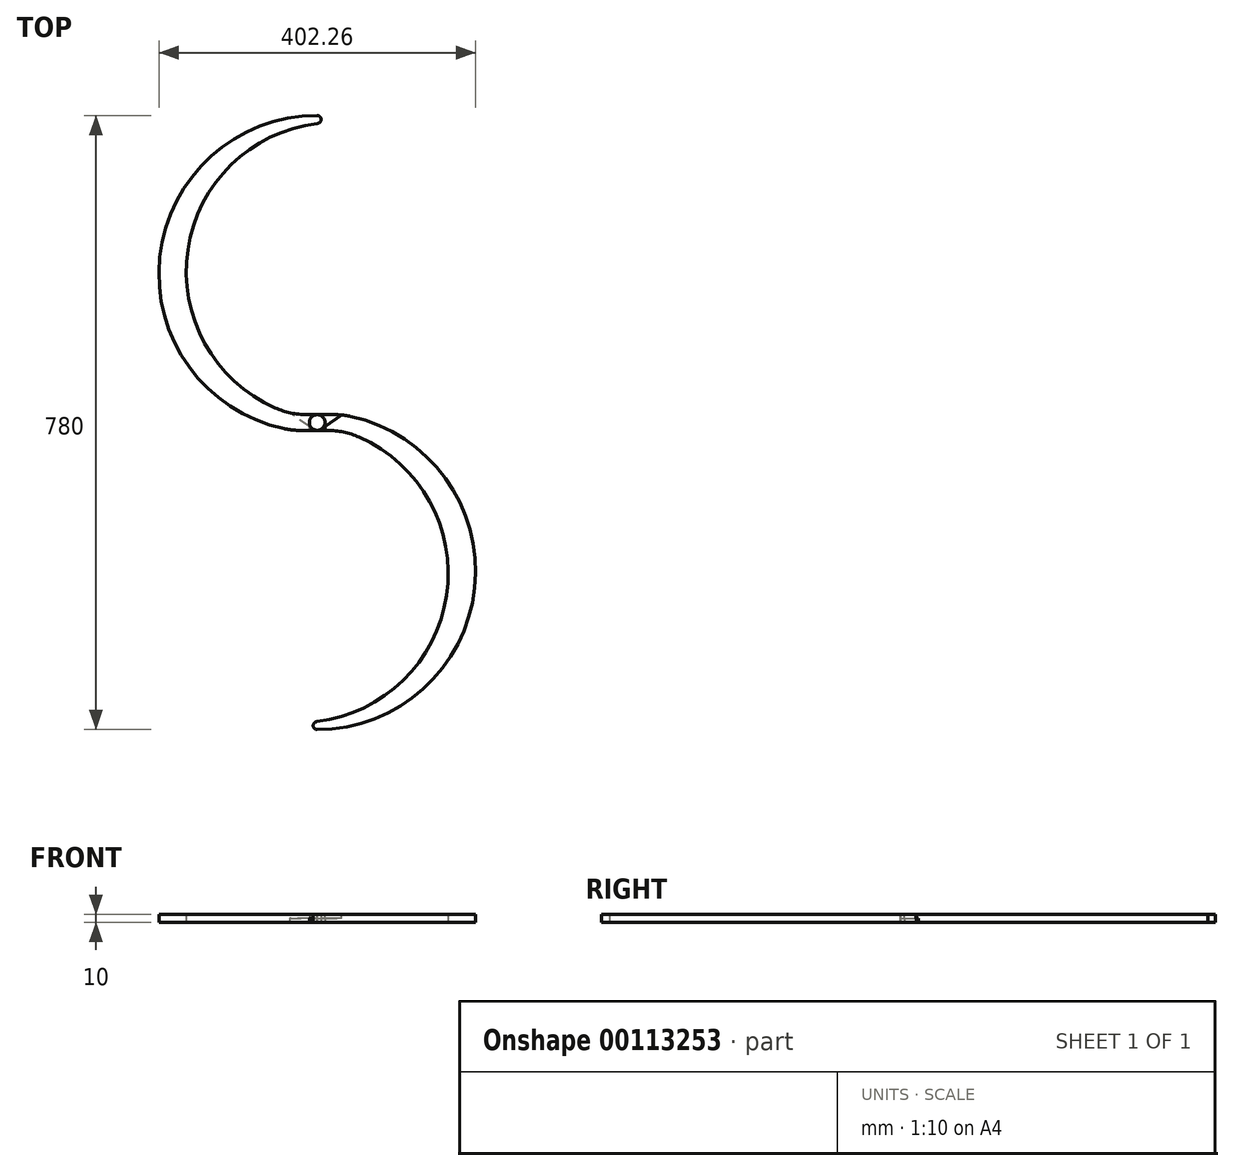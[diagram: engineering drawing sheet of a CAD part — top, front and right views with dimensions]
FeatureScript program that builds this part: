
annotation { "Feature Type Name" : "Feature", "Feature Type Description" : "" }
export const myFeature = defineFeature(function(context is Context, id is Id, definition is map)
    precondition{}
    {
        {
            var Q0;
            Q0=qCreatedBy(makeId("Top.planeOp"),FACE);
            var sketch = newSketch(context, id + "F0", { "sketchPlane" : qUnion([Q0])});
            skArc(sketch, "E0", {"start": v(0, 390) * mm, "mid": v(-200, 210.09) * mm, "end": v(-42.2, -7.78) * mm});
            skLineSegment(sketch, "E1", {"start": v(-21.21, -10) * mm, "end": v(0, -10) * mm});
            skLineSegment(sketch, "E2", {"start": v(0, -10) * mm, "end": v(0, 10) * mm, "construction": true});
            skPoint(sketch, "E3", {"position": v(0, 0) * mm});
            skLineSegment(sketch, "E4", {"start": v(0, 10) * mm, "end": v(-12.94, 10) * mm});
            skArc(sketch, "E5", {"start": v(0, 380) * mm, "mid": v(-164.3, 219.56) * mm, "end": v(-53.31, 18.51) * mm});
            skArc(sketch, "E6", {"start": v(0, 380) * mm, "mid": v(5, 385) * mm, "end": v(0, 390) * mm});
            skArc(sketch, "E7.1.0", {"start": v(0, -390) * mm, "mid": v(200, -210.09) * mm, "end": v(42.2, 7.78) * mm});
            skArc(sketch, "E7.1.1", {"start": v(0, -380) * mm, "mid": v(164.3, -219.56) * mm, "end": v(53.31, -18.51) * mm});
            skArc(sketch, "E7.1.2", {"start": v(0, -380) * mm, "mid": v(-5, -385) * mm, "end": v(0, -390) * mm});
            skLineSegment(sketch, "E7.1.3", {"start": v(0, -10) * mm, "end": v(12.94, -10) * mm});
            skLineSegment(sketch, "E7.1.4", {"start": v(21.21, 10) * mm, "end": v(0, 10) * mm});
            skPoint(sketch, "E8.visualSharp", {"position": v(-30, 10) * mm});
            skArc(sketch, "E8.filletArc", {"start": v(-53.31, 18.51) * mm, "mid": v(-33.57, 12.15) * mm, "end": v(-12.94, 10) * mm});
            skPoint(sketch, "E9.visualSharp", {"position": v(30, 10) * mm});
            skArc(sketch, "E9.filletArc", {"start": v(42.2, 7.78) * mm, "mid": v(31.76, 9.44) * mm, "end": v(21.21, 10) * mm});
            skPoint(sketch, "E10.visualSharp", {"position": v(-30, -10) * mm});
            skArc(sketch, "E10.filletArc", {"start": v(-42.2, -7.78) * mm, "mid": v(-31.76, -9.44) * mm, "end": v(-21.21, -10) * mm});
            skPoint(sketch, "E11.visualSharp", {"position": v(30, -10) * mm});
            skArc(sketch, "E11.filletArc", {"start": v(53.31, -18.51) * mm, "mid": v(33.57, -12.15) * mm, "end": v(12.94, -10) * mm});
            skLineSegment(sketch, "E12.bottom", {"start": v(47.12, -23.38) * mm, "end": v(-234.9, -23.38) * mm, "construction": true});
            skLineSegment(sketch, "E12.top", {"start": v(47.12, 411.9) * mm, "end": v(-234.9, 411.9) * mm, "construction": true});
            skLineSegment(sketch, "E12.left", {"start": v(47.12, -23.38) * mm, "end": v(47.12, 411.9) * mm, "construction": true});
            skLineSegment(sketch, "E12.right", {"start": v(-234.9, -23.38) * mm, "end": v(-234.9, 411.9) * mm, "construction": true});
            skSolve(sketch);
        }
        {
            var Q0;
            Q0=qSketchRegion(id+"F0",true);
            extrude(context, id + "F1", {"entities" : qUnion([Q0]), "depth" : 10 * mm});
        }
        {
            var Q0;
            Q0=makeQuery(id+"F1.opExtrude","CAP_FACE",FACE,{"disambiguationData":[OSD([sQuery(id+"F0.wireOp",EDGE,"E0"),sQuery(id+"F0.wireOp",EDGE,"E1"),sQuery(id+"F0.wireOp",EDGE,"E4"),sQuery(id+"F0.wireOp",EDGE,"E5"),sQuery(id+"F0.wireOp",EDGE,"E6"),sQuery(id+"F0.wireOp",EDGE,"E7.1.0"),sQuery(id+"F0.wireOp",EDGE,"E7.1.1"),sQuery(id+"F0.wireOp",EDGE,"E7.1.2"),sQuery(id+"F0.wireOp",EDGE,"E7.1.3"),sQuery(id+"F0.wireOp",EDGE,"E7.1.4"),sQuery(id+"F0.wireOp",EDGE,"E8.filletArc"),sQuery(id+"F0.wireOp",EDGE,"E9.filletArc"),sQuery(id+"F0.wireOp",EDGE,"E10.filletArc"),sQuery(id+"F0.wireOp",EDGE,"E11.filletArc")])],"isStart":false});
            var sketch = newSketch(context, id + "F2", { "sketchPlane" : qUnion([Q0])});
            skCircle(sketch, "E13", {"center": v(0, 0) * mm, "radius": 3 * mm});
            skArc(sketch, "E14", {"start": v(0, -10) * mm, "mid": v(10, 0) * mm, "end": v(0, 10) * mm});
            skLineSegment(sketch, "E15.0", {"start": v(21.21, 10) * mm, "end": v(-12.94, 10) * mm});
            skArc(sketch, "E16.0", {"start": v(42.2, 7.78) * mm, "mid": v(31.76, 9.44) * mm, "end": v(21.21, 10) * mm});
            skArc(sketch, "E17.0", {"start": v(0, -390) * mm, "mid": v(200, -210.09) * mm, "end": v(42.2, 7.78) * mm});
            skArc(sketch, "E18.0", {"start": v(0, -380) * mm, "mid": v(-5, -385) * mm, "end": v(0, -390) * mm});
            skArc(sketch, "E19.0", {"start": v(0, -380) * mm, "mid": v(164.3, -219.56) * mm, "end": v(53.31, -18.51) * mm});
            skArc(sketch, "E20.0", {"start": v(53.31, -18.51) * mm, "mid": v(33.57, -12.15) * mm, "end": v(12.94, -10) * mm});
            skLineSegment(sketch, "E21.0", {"start": v(-21.21, -10) * mm, "end": v(12.94, -10) * mm});
            skSolve(sketch);
        }
        {
            var Q0;
            Q0 = qSketchRegion(id + "F2", true);
            extrude(context, id + "F3", {"entities" : qUnion([Q0]), "operationType" : NewBodyOperationType.REMOVE, "oppositeDirection" : true, "depth" : 25 * mm});
        }
        {
            var Q0;
            Q0=makeQuery(id+"F1.opExtrude","SWEPT_BODY",BODY,{"disambiguationData":[OSD([sQuery(id+"F0.wireOp",EDGE,"E0"),sQuery(id+"F0.wireOp",EDGE,"E1"),sQuery(id+"F0.wireOp",EDGE,"E4"),sQuery(id+"F0.wireOp",EDGE,"E5"),sQuery(id+"F0.wireOp",EDGE,"E6"),sQuery(id+"F0.wireOp",EDGE,"E7.1.0"),sQuery(id+"F0.wireOp",EDGE,"E7.1.1"),sQuery(id+"F0.wireOp",EDGE,"E7.1.2"),sQuery(id+"F0.wireOp",EDGE,"E7.1.3"),sQuery(id+"F0.wireOp",EDGE,"E7.1.4"),sQuery(id+"F0.wireOp",EDGE,"E8.filletArc"),sQuery(id+"F0.wireOp",EDGE,"E9.filletArc"),sQuery(id+"F0.wireOp",EDGE,"E10.filletArc"),sQuery(id+"F0.wireOp",EDGE,"E11.filletArc")])]});
            var Q1;
            Q1=qCreatedBy(makeId("Right.planeOp"),FACE);
            mirror(context, id + "F4", {"entities" : qUnion([Q0]), "mirrorPlane" : qUnion([Q1])});
        }
        {
            var Q0;
            Q0=makeQuery(id+"F1.opExtrude","CAP_FACE",FACE,{"disambiguationData":[OSD([sQuery(id+"F0.wireOp",EDGE,"E0"),sQuery(id+"F0.wireOp",EDGE,"E1"),sQuery(id+"F0.wireOp",EDGE,"E4"),sQuery(id+"F0.wireOp",EDGE,"E5"),sQuery(id+"F0.wireOp",EDGE,"E6"),sQuery(id+"F0.wireOp",EDGE,"E7.1.0"),sQuery(id+"F0.wireOp",EDGE,"E7.1.1"),sQuery(id+"F0.wireOp",EDGE,"E7.1.2"),sQuery(id+"F0.wireOp",EDGE,"E7.1.3"),sQuery(id+"F0.wireOp",EDGE,"E7.1.4"),sQuery(id+"F0.wireOp",EDGE,"E8.filletArc"),sQuery(id+"F0.wireOp",EDGE,"E9.filletArc"),sQuery(id+"F0.wireOp",EDGE,"E10.filletArc"),sQuery(id+"F0.wireOp",EDGE,"E11.filletArc")])],"isStart":true});
            var sketch = newSketch(context, id + "F5", { "sketchPlane" : qUnion([Q0])});
            skCircle(sketch, "E22", {"center": v(0, 0) * mm, "radius": 10 * mm});
            skLineSegment(sketch, "E23", {"start": v(-5.74, 8.2) * mm, "end": v(-35.35, -12.54) * mm});
            skArc(sketch, "E24.0", {"start": v(-53.31, -18.51) * mm, "mid": v(-33.57, -12.15) * mm, "end": v(-12.94, -10) * mm});
            skLineSegment(sketch, "E25.0", {"start": v(0, -10) * mm, "end": v(-12.94, -10) * mm});
            skSolve(sketch);
        }
        {
            var Q0;
            Q0 = qSketchRegion(id + "F5", true);
            extrude(context, id + "F6", {"entities" : qUnion([Q0]), "operationType" : NewBodyOperationType.REMOVE, "oppositeDirection" : true, "depth" : 5 * mm});
        }
        {
            var Q0;
            Q0=makeQuery(id+"F4.opPattern","COPY",BODY,{"derivedFrom":makeQuery(id+"F1.opExtrude","SWEPT_BODY",BODY,{"disambiguationData":[OSD([sQuery(id+"F0.wireOp",EDGE,"E0"),sQuery(id+"F0.wireOp",EDGE,"E1"),sQuery(id+"F0.wireOp",EDGE,"E4"),sQuery(id+"F0.wireOp",EDGE,"E5"),sQuery(id+"F0.wireOp",EDGE,"E6"),sQuery(id+"F0.wireOp",EDGE,"E7.1.0"),sQuery(id+"F0.wireOp",EDGE,"E7.1.1"),sQuery(id+"F0.wireOp",EDGE,"E7.1.2"),sQuery(id+"F0.wireOp",EDGE,"E7.1.3"),sQuery(id+"F0.wireOp",EDGE,"E7.1.4"),sQuery(id+"F0.wireOp",EDGE,"E8.filletArc"),sQuery(id+"F0.wireOp",EDGE,"E9.filletArc"),sQuery(id+"F0.wireOp",EDGE,"E10.filletArc"),sQuery(id+"F0.wireOp",EDGE,"E11.filletArc")])]}),"instanceName":"1"});
            var Q1;
            Q1=qCreatedBy(makeId("Front.planeOp"),FACE);
            mirror(context, id + "F7", {"entities" : qUnion([Q0]), "mirrorPlane" : qUnion([Q1])});
        }
        {
            var Q0;
            Q0=makeQuery(id+"F4.opPattern","COPY",BODY,{"derivedFrom":makeQuery(id+"F1.opExtrude","SWEPT_BODY",BODY,{"disambiguationData":[OSD([sQuery(id+"F0.wireOp",EDGE,"E0"),sQuery(id+"F0.wireOp",EDGE,"E1"),sQuery(id+"F0.wireOp",EDGE,"E4"),sQuery(id+"F0.wireOp",EDGE,"E5"),sQuery(id+"F0.wireOp",EDGE,"E6"),sQuery(id+"F0.wireOp",EDGE,"E7.1.0"),sQuery(id+"F0.wireOp",EDGE,"E7.1.1"),sQuery(id+"F0.wireOp",EDGE,"E7.1.2"),sQuery(id+"F0.wireOp",EDGE,"E7.1.3"),sQuery(id+"F0.wireOp",EDGE,"E7.1.4"),sQuery(id+"F0.wireOp",EDGE,"E8.filletArc"),sQuery(id+"F0.wireOp",EDGE,"E9.filletArc"),sQuery(id+"F0.wireOp",EDGE,"E10.filletArc"),sQuery(id+"F0.wireOp",EDGE,"E11.filletArc")])]}),"instanceName":"1"});
            deleteBodies(context, id + "F8", {"entities" : qUnion([Q0])});
        }
        {
            var Q0;
            Q0=makeQuery(id+"F7.opPattern","COPY",FACE,{"derivedFrom":makeQuery(id+"F4.opPattern","COPY",FACE,{"derivedFrom":makeQuery(id+"F1.opExtrude","CAP_FACE",FACE,{"disambiguationData":[OSD([sQuery(id+"F0.wireOp",EDGE,"E0"),sQuery(id+"F0.wireOp",EDGE,"E1"),sQuery(id+"F0.wireOp",EDGE,"E4"),sQuery(id+"F0.wireOp",EDGE,"E5"),sQuery(id+"F0.wireOp",EDGE,"E6"),sQuery(id+"F0.wireOp",EDGE,"E7.1.0"),sQuery(id+"F0.wireOp",EDGE,"E7.1.1"),sQuery(id+"F0.wireOp",EDGE,"E7.1.2"),sQuery(id+"F0.wireOp",EDGE,"E7.1.3"),sQuery(id+"F0.wireOp",EDGE,"E7.1.4"),sQuery(id+"F0.wireOp",EDGE,"E8.filletArc"),sQuery(id+"F0.wireOp",EDGE,"E9.filletArc"),sQuery(id+"F0.wireOp",EDGE,"E10.filletArc"),sQuery(id+"F0.wireOp",EDGE,"E11.filletArc")])],"isStart":false}),"instanceName":"1"}),"instanceName":"1"});
            var sketch = newSketch(context, id + "F9", { "sketchPlane" : qUnion([Q0])});
            skCircle(sketch, "E26", {"center": v(0, 0) * mm, "radius": 10 * mm});
            skLineSegment(sketch, "E27", {"start": v(5.74, -8.2) * mm, "end": v(31.03, 9.52) * mm});
            skLineSegment(sketch, "E28.0", {"start": v(21.21, 10) * mm, "end": v(0, 10) * mm});
            skArc(sketch, "E29.0", {"start": v(42.2, 7.78) * mm, "mid": v(31.76, 9.44) * mm, "end": v(21.21, 10) * mm});
            skSolve(sketch);
        }
        {
            var Q0;
            Q0 = qSketchRegion(id + "F9", true);
            extrude(context, id + "F10", {"entities" : qUnion([Q0]), "operationType" : NewBodyOperationType.REMOVE, "oppositeDirection" : true, "depth" : 5 * mm});
        }
        {
            var Q0;
            Q0=makeQuery(id+"F7.opPattern","COPY",FACE,{"derivedFrom":makeQuery(id+"F4.opPattern","COPY",FACE,{"derivedFrom":makeQuery(id+"F1.opExtrude","CAP_FACE",FACE,{"disambiguationData":[OSD([sQuery(id+"F0.wireOp",EDGE,"E0"),sQuery(id+"F0.wireOp",EDGE,"E1"),sQuery(id+"F0.wireOp",EDGE,"E4"),sQuery(id+"F0.wireOp",EDGE,"E5"),sQuery(id+"F0.wireOp",EDGE,"E6"),sQuery(id+"F0.wireOp",EDGE,"E7.1.0"),sQuery(id+"F0.wireOp",EDGE,"E7.1.1"),sQuery(id+"F0.wireOp",EDGE,"E7.1.2"),sQuery(id+"F0.wireOp",EDGE,"E7.1.3"),sQuery(id+"F0.wireOp",EDGE,"E7.1.4"),sQuery(id+"F0.wireOp",EDGE,"E8.filletArc"),sQuery(id+"F0.wireOp",EDGE,"E9.filletArc"),sQuery(id+"F0.wireOp",EDGE,"E10.filletArc"),sQuery(id+"F0.wireOp",EDGE,"E11.filletArc")])],"isStart":true}),"instanceName":"1"}),"instanceName":"1"});
            var sketch = newSketch(context, id + "F11", { "sketchPlane" : qUnion([Q0])});
            skLineSegment(sketch, "E30", {"start": v(0, 10) * mm, "end": v(-10, 10) * mm});
            skPoint(sketch, "E30.endSnap0", {"position": v(-10, 0) * mm});
            skLineSegment(sketch, "E31", {"start": v(-10, 10) * mm, "end": v(-10, 0) * mm});
            skArc(sketch, "E32.0", {"start": v(0, -10) * mm, "mid": v(-10, 0) * mm, "end": v(0, 10) * mm});
            skSolve(sketch);
        }
        {
            var Q0;
            Q0 = qSketchRegion(id + "F11", true);
            extrude(context, id + "F12", {"entities" : qUnion([Q0]), "operationType" : NewBodyOperationType.ADD, "oppositeDirection" : true, "depth" : 5 * mm});
        }
        {
            var Q0;
            {var subQ0=sQuery(id+"F11.wireOp",EDGE,"E30");Q0=makeQuery(id+"F11.imprint","IMPRINT",FACE,{"disambiguationData":[TD([[makeQuery(id+"F11.imprint","IMPRINT",EDGE,{"derivedFrom":subQ0}),1.0]])]});}
            extrude(context, id + "F13", {"entities" : qUnion([Q0]), "operationType" : NewBodyOperationType.REMOVE, "oppositeDirection" : true, "depth" : 5 * mm});
        }
        {
            var Q0;
            Q0=makeQuery(id+"F1.opExtrude","CAP_FACE",FACE,{"disambiguationData":[OSD([sQuery(id+"F0.wireOp",EDGE,"E0"),sQuery(id+"F0.wireOp",EDGE,"E1"),sQuery(id+"F0.wireOp",EDGE,"E4"),sQuery(id+"F0.wireOp",EDGE,"E5"),sQuery(id+"F0.wireOp",EDGE,"E6"),sQuery(id+"F0.wireOp",EDGE,"E7.1.0"),sQuery(id+"F0.wireOp",EDGE,"E7.1.1"),sQuery(id+"F0.wireOp",EDGE,"E7.1.2"),sQuery(id+"F0.wireOp",EDGE,"E7.1.3"),sQuery(id+"F0.wireOp",EDGE,"E7.1.4"),sQuery(id+"F0.wireOp",EDGE,"E8.filletArc"),sQuery(id+"F0.wireOp",EDGE,"E9.filletArc"),sQuery(id+"F0.wireOp",EDGE,"E10.filletArc"),sQuery(id+"F0.wireOp",EDGE,"E11.filletArc")])],"isStart":false});
            var sketch = newSketch(context, id + "F14", { "sketchPlane" : qUnion([Q0])});
            skLineSegment(sketch, "E33", {"start": v(0, -10) * mm, "end": v(10, -10) * mm});
            skPoint(sketch, "E33.endSnap0", {"position": v(10, 0) * mm});
            skLineSegment(sketch, "E34", {"start": v(10, -10) * mm, "end": v(10, 0) * mm});
            skArc(sketch, "E35.0", {"start": v(0, -10) * mm, "mid": v(10, 0) * mm, "end": v(0, 10) * mm});
            skSolve(sketch);
        }
        {
            var Q0;
            Q0 = qSketchRegion(id + "F14", true);
            extrude(context, id + "F15", {"entities" : qUnion([Q0]), "operationType" : NewBodyOperationType.ADD, "oppositeDirection" : true, "depth" : 5 * mm});
        }
        {
            var Q0;
            {var subQ0=sQuery(id+"F14.wireOp",EDGE,"E33");Q0=makeQuery(id+"F14.imprint","IMPRINT",FACE,{"disambiguationData":[TD([[makeQuery(id+"F14.imprint","IMPRINT",EDGE,{"derivedFrom":subQ0}),1.0]])]});}
            extrude(context, id + "F16", {"entities" : qUnion([Q0]), "operationType" : NewBodyOperationType.REMOVE, "oppositeDirection" : true, "depth" : 5 * mm});
        }
    });
